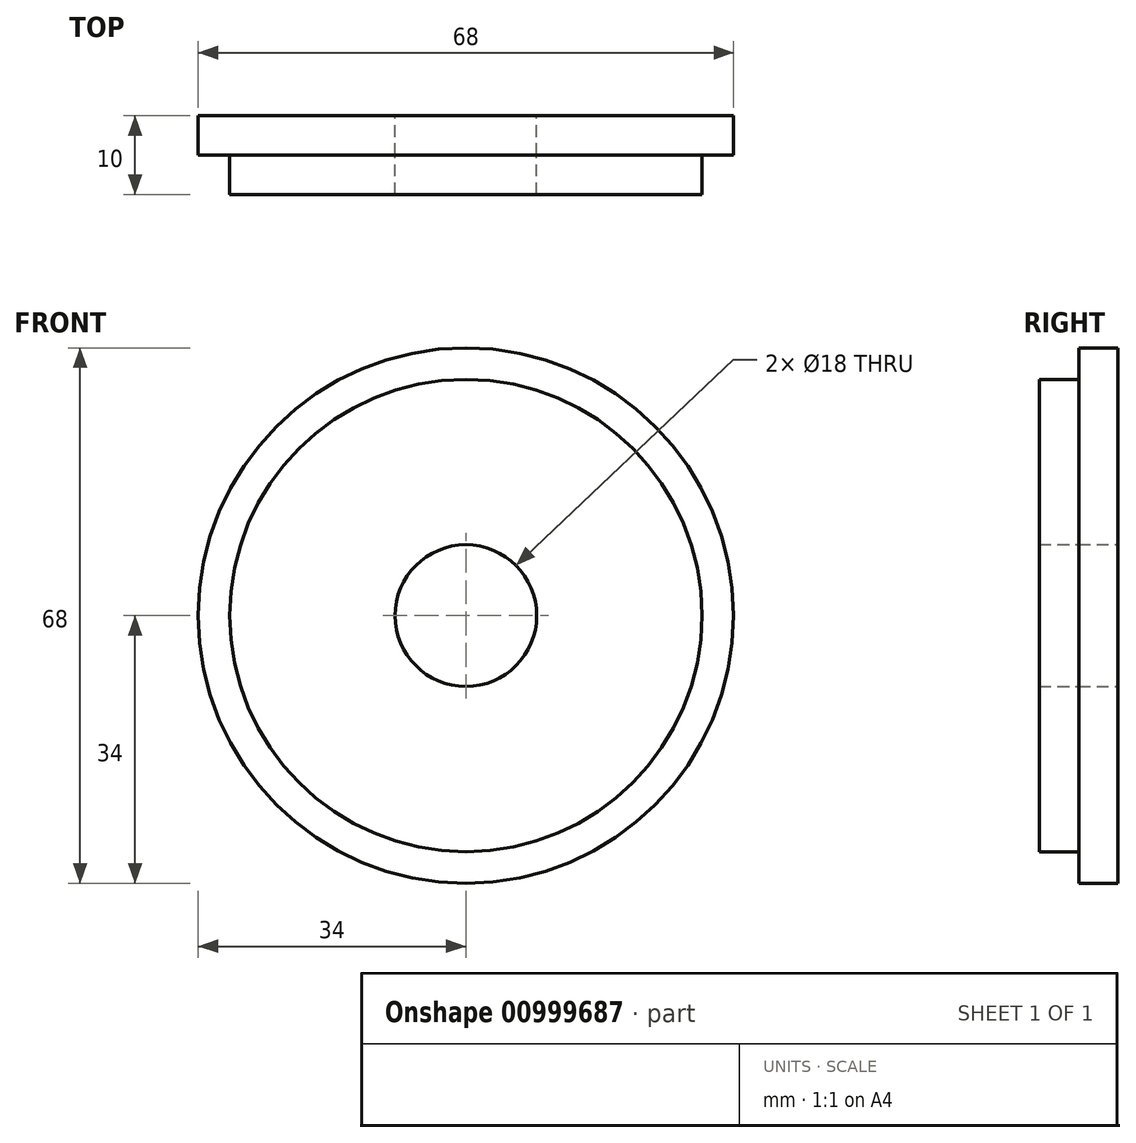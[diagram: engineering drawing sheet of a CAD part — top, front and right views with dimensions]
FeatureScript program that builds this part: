
annotation { "Feature Type Name" : "Feature", "Feature Type Description" : "" }
export const myFeature = defineFeature(function(context is Context, id is Id, definition is map)
    precondition{}
    {
        {
            var Q0;
            Q0=qCreatedBy(makeId("Front.planeOp"),FACE);
            var sketch = newSketch(context, id + "F0", { "sketchPlane" : qUnion([Q0])});
            skCircle(sketch, "E0", {"center": v(0, 0) * mm, "radius": 34 * mm});
            skSolve(sketch);
        }
        {
            var Q0;
            Q0 = qSketchRegion(id + "F0", true);
            extrude(context, id + "F1", {"entities" : qUnion([Q0]), "depth" : 5 * mm, "offsetDistance" : 25 * mm});
        }
        {
            var Q0;
            Q0=makeQuery(id+"F1.opExtrude","CAP_FACE",FACE,{"disambiguationData":[OSD([sQuery(id+"F0.wireOp",EDGE,"E0")])],"isStart":false});
            cPlane(context, id + "F2", {"entities" : qUnion([Q0]), "cplaneType" : CPlaneType.OFFSET, "offset" : 0 * mm, "width" : 150 * mm, "height" : 150 * mm});
        }
        {
            var Q0;
            Q0=qCreatedBy(id+"F2.planeOp",FACE);
            var sketch = newSketch(context, id + "F3", { "sketchPlane" : qUnion([Q0])});
            skCircle(sketch, "E1", {"center": v(0, 0) * mm, "radius": 30 * mm});
            skSolve(sketch);
        }
        {
            var Q0;
            Q0 = qSketchRegion(id + "F3", true);
            extrude(context, id + "F4", {"entities" : qUnion([Q0]), "depth" : 5 * mm, "offsetDistance" : 25 * mm});
        }
        {
            var Q0;
            Q0=makeQuery(id+"F1.opExtrude","CAP_FACE",FACE,{"disambiguationData":[OSD([sQuery(id+"F0.wireOp",EDGE,"E0")])],"isStart":true});
            var sketch = newSketch(context, id + "F5", { "sketchPlane" : qUnion([Q0])});
            skCircle(sketch, "E2", {"center": v(0, 0) * mm, "radius": 9 * mm});
            skSolve(sketch);
        }
        {
            var Q0;
            Q0 = qSketchRegion(id + "F5", true);
            extrude(context, id + "F6", {"entities" : qUnion([Q0]), "operationType" : NewBodyOperationType.REMOVE, "oppositeDirection" : true, "depth" : 56.2 * mm, "offsetDistance" : 25 * mm});
        }
        {
            var Q0;
            Q0=makeQuery(id+"F4.opExtrude","CAP_FACE",FACE,{"disambiguationData":[OSD([sQuery(id+"F3.wireOp",EDGE,"E1")])],"isStart":true});
            var sketch = newSketch(context, id + "F7", { "sketchPlane" : qUnion([Q0])});
            skCircle(sketch, "E3", {"center": v(0, 0) * mm, "radius": 9 * mm});
            skSolve(sketch);
        }
        {
            var Q0;
            Q0 = qSketchRegion(id + "F7", true);
            extrude(context, id + "F8", {"entities" : qUnion([Q0]), "operationType" : NewBodyOperationType.REMOVE, "oppositeDirection" : true, "depth" : 25 * mm, "offsetDistance" : 25 * mm});
        }
    });
